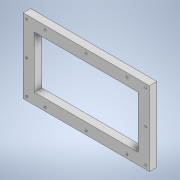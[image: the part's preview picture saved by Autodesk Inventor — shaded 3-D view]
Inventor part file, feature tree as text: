
AUTODESK INVENTOR PART (.ipt)
format: ipt  version: 2022.2 (Build 262287030, 287C)  size: 162,304 bytes
history: native  units: in
note: dims shown in document units (in); Inventor stores cm internally (conversion verified against a paired STEP export)
features: sketch x3, extrude x2, hole x2
ambient origin geometry x8: Origin, YZ Plane, XZ Plane, XY Plane, X Axis, Y Axis, Z Axis, Center Point
bodies: Solid1 (feature_tree)
feature tree (7):
  extrude  "Extrusion1"  Depth=3.937in
  extrude  "Extrusion2"  Depth=5.5118in
  hole  "Hole1"  [1 undecoded]
  hole  "Hole2"  [1 undecoded]
  sketch  "Sketch1"  dims[d0=6.6929in d1=3.937in]
  sketch  "Sketch2"  dims[d2=0.3937in d3=0.0in d4=5.5118in]
  sketch  "Sketch4"  dims[d5=2.7559in d6=0.3937in d7=0.0in d38=0.125in d39=0.2953in d40=0.1476in d41=0.0984in d42=90.0deg d43=0.1969in d44=0.0in d45=0.1969in d53=0.7874in d55=1.9685in d56=0.3937in d58=0.3937in d60=0.7874in d62=6.2992in d63=0.3937in d65=0.3937in d72=1.9685in d73=0.1969in d74=0.1969in d75=3.3465in d78=0.9843in d80=0.1969in d81=0.1969in d82=0.9843in d83=0.7874in d85=6.2992in d86=0.3937in d88=0.3937in d106=0.0984in d107=0.2953in d108=0.1476in d109=0.0984in d110=90.0deg d111=0.1181in d112=0.0in d115=0.1969in d116=0.1969in d117=0.1969in d118=0.7874in d120=3.5433in d121=0.3937in d123=0.3937in d125=1.7717in d131=0.9843in d156=2.2638in d157=0.7874in d159=2.1654in d160=0.7874in d162=3.5433in d158=0.3937in d161=0.1476in d163=0.2953in d164=0.8108in d165=0.0246in d166=0.2953in d167=0.1476in d168=0.0591in d169=0.0984in d170=0.1476in d171=0.5635in d172=0.2953in d173=0.8108in d174=0.0246in d175=0.2953in d176=0.1476in]
note: 2 required parameter values undecoded (feature->parameter linkage not recoverable at this tier; creation-order binding heuristic only, values carry confidence <= 0.55)
